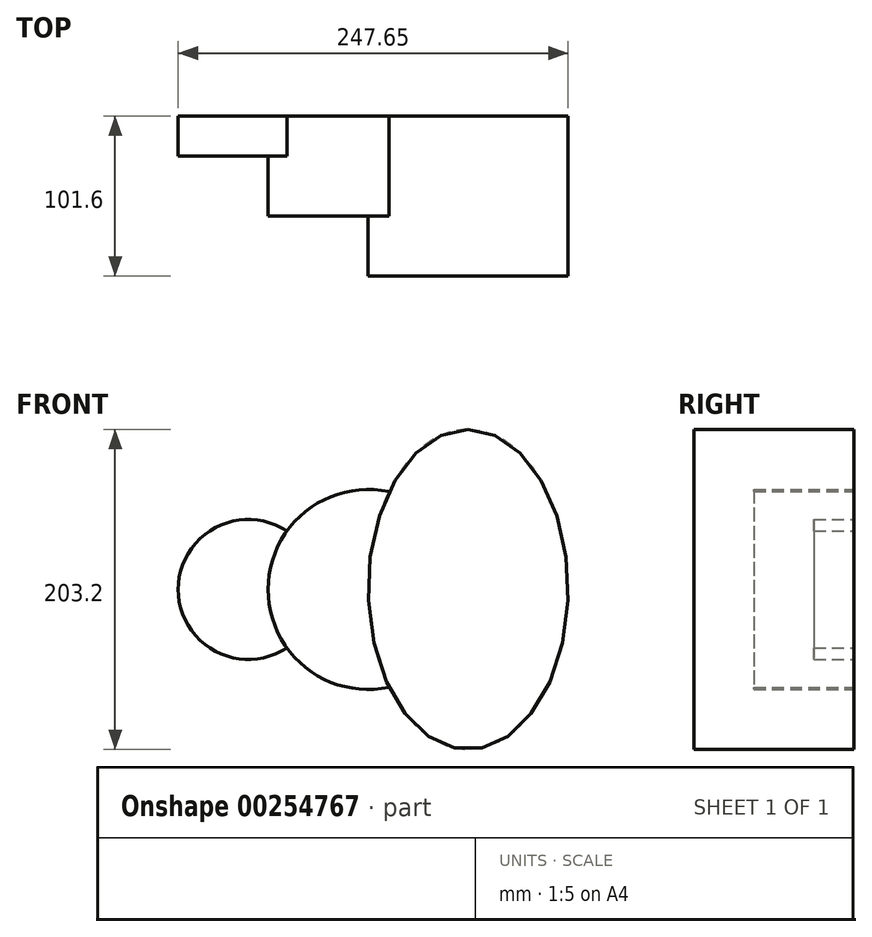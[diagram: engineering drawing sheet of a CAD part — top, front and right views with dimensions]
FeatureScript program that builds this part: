
annotation { "Feature Type Name" : "Feature", "Feature Type Description" : "" }
export const myFeature = defineFeature(function(context is Context, id is Id, definition is map)
    precondition{}
    {
        {
            var Q0;
            Q0=qCreatedBy(makeId("Front.planeOp"),FACE);
            var sketch = newSketch(context, id + "F0", { "sketchPlane" : qUnion([Q0])});
            skCircle(sketch, "E0", {"center": v(-76.2, 0) * mm, "radius": 44.45 * mm});
            skCircle(sketch, "E1", {"center": v(0, 0) * mm, "radius": 63.5 * mm});
            skEllipse(sketch, "E2", {"center": v(63.5, 0) * mm, "majorRadius": 101.6 * mm, "minorRadius": 63.5 * mm, "majorAxis": v(0, 1)});
            skSolve(sketch);
        }
        {
            var Q0;
            {var subQ0=sQuery(id+"F0.wireOp",EDGE,"E1");var subQ1=sQuery(id+"F0.wireOp",EDGE,"E0");var subQ2=makeQuery(id+"F0.imprint","INTERSECT",VERTEX,{"disambiguationData":[OD(0.0)],"derivedFrom":[subQ1,subQ0]});Q0=makeQuery(id+"F0.imprint","IMPRINT",FACE,{"disambiguationData":[TD([[makeQuery(id+"F0.imprint","IMPRINT",EDGE,{"disambiguationData":[TD([[subQ2,-1.0]])],"derivedFrom":subQ1}),1.0]])]});}
            extrude(context, id + "F1", {"entities" : qUnion([Q0]), "depth" : 25.4 * mm});
        }
        {
            var Q0;
            {var subQ0=sQuery(id+"F0.wireOp",EDGE,"E1");var subQ1=sQuery(id+"F0.wireOp",EDGE,"E0");var subQ2=makeQuery(id+"F0.imprint","INTERSECT",VERTEX,{"disambiguationData":[OD(0.0)],"derivedFrom":[subQ1,subQ0]});Q0=makeQuery(id+"F0.imprint","IMPRINT",FACE,{"disambiguationData":[TD([[makeQuery(id+"F0.imprint","IMPRINT",EDGE,{"disambiguationData":[TD([[subQ2,1.0]])],"derivedFrom":subQ1}),-1.0]])]});}
            var Q1;
            {var subQ0=sQuery(id+"F0.wireOp",EDGE,"E1");var subQ1=sQuery(id+"F0.wireOp",EDGE,"E0");var subQ2=makeQuery(id+"F0.imprint","INTERSECT",VERTEX,{"disambiguationData":[OD(0.0)],"derivedFrom":[subQ1,subQ0]});Q1=makeQuery(id+"F0.imprint","IMPRINT",FACE,{"disambiguationData":[TD([[makeQuery(id+"F0.imprint","IMPRINT",EDGE,{"disambiguationData":[TD([[subQ2,1.0]])],"derivedFrom":subQ1}),1.0]])]});}
            extrude(context, id + "F2", {"entities" : qUnion([Q0, Q1]), "operationType" : NewBodyOperationType.ADD, "depth" : 63.5 * mm});
        }
        {
            var Q0;
            {var subQ0=sQuery(id+"F0.wireOp",EDGE,"E2");var subQ1=sQuery(id+"F0.wireOp",EDGE,"E1");var subQ2=makeQuery(id+"F0.imprint","INTERSECT",VERTEX,{"disambiguationData":[OD(0.0)],"derivedFrom":[subQ1,subQ0]});Q0=makeQuery(id+"F0.imprint","IMPRINT",FACE,{"disambiguationData":[TD([[makeQuery(id+"F0.imprint","IMPRINT",EDGE,{"disambiguationData":[TD([[subQ2,1.0]])],"derivedFrom":subQ1}),-1.0]])]});}
            var Q1;
            {var subQ0=sQuery(id+"F0.wireOp",EDGE,"E2");var subQ1=sQuery(id+"F0.wireOp",EDGE,"E1");var subQ2=makeQuery(id+"F0.imprint","INTERSECT",VERTEX,{"disambiguationData":[OD(0.0)],"derivedFrom":[subQ1,subQ0]});Q1=makeQuery(id+"F0.imprint","IMPRINT",FACE,{"disambiguationData":[TD([[makeQuery(id+"F0.imprint","IMPRINT",EDGE,{"disambiguationData":[TD([[subQ2,1.0]])],"derivedFrom":subQ1}),1.0]])]});}
            extrude(context, id + "F3", {"entities" : qUnion([Q0, Q1]), "operationType" : NewBodyOperationType.ADD, "depth" : 101.6 * mm});
        }
    });
